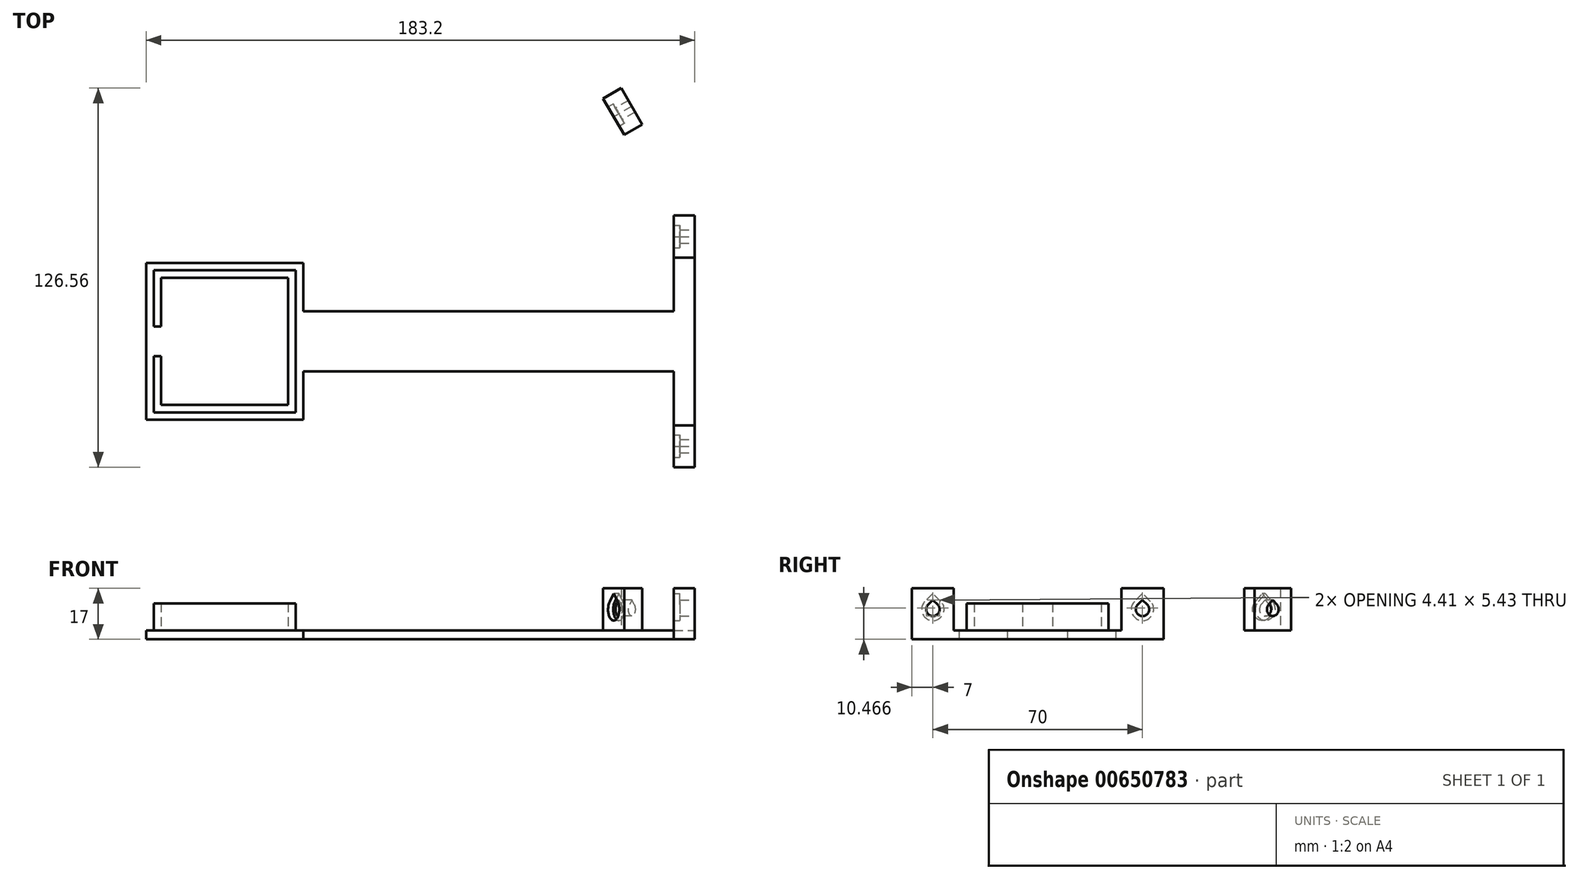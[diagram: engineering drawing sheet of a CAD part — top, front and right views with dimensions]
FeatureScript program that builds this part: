
annotation { "Feature Type Name" : "Feature", "Feature Type Description" : "" }
export const myFeature = defineFeature(function(context is Context, id is Id, definition is map)
    precondition{}
    {
        {
            var Q0;
            Q0=qCreatedBy(makeId("Top.planeOp"),FACE);
            var sketch = newSketch(context, id + "F0", { "sketchPlane" : qUnion([Q0])});
            skLineSegment(sketch, "E0.bottom", {"start": v(21.2, 21.2) * mm, "end": v(-21.2, 21.2) * mm});
            skLineSegment(sketch, "E0.top", {"start": v(21.2, -21.2) * mm, "end": v(-21.2, -21.2) * mm});
            skLineSegment(sketch, "E0.left", {"start": v(21.2, 21.2) * mm, "end": v(21.2, -21.2) * mm});
            skLineSegment(sketch, "E0.right", {"start": v(-21.2, 21.2) * mm, "end": v(-21.2, -21.2) * mm});
            skPoint(sketch, "E0.middle", {"position": v(0, 0) * mm});
            skLineSegment(sketch, "E1.bottom", {"start": v(23.7, 23.7) * mm, "end": v(-23.7, 23.7) * mm});
            skLineSegment(sketch, "E1.top", {"start": v(23.7, -23.7) * mm, "end": v(-23.7, -23.7) * mm});
            skLineSegment(sketch, "E1.left", {"start": v(23.7, 23.7) * mm, "end": v(23.7, -23.7) * mm});
            skLineSegment(sketch, "E1.right", {"start": v(-23.7, 23.7) * mm, "end": v(-23.7, -23.7) * mm});
            skLineSegment(sketch, "E2", {"start": v(0, 0) * mm, "end": v(-23.7, 0) * mm});
            skLineSegment(sketch, "E3", {"start": v(-23.7, 0) * mm, "end": v(-23.7, 5) * mm});
            skLineSegment(sketch, "E4", {"start": v(-21.2, 0) * mm, "end": v(-21.2, -5) * mm});
            skLineSegment(sketch, "E5.bottom", {"start": v(-23.7, 5) * mm, "end": v(-21.2, 5) * mm});
            skLineSegment(sketch, "E5.top", {"start": v(-23.7, -5) * mm, "end": v(-21.2, -5) * mm});
            skLineSegment(sketch, "E5.left", {"start": v(-23.7, 5) * mm, "end": v(-23.7, -5) * mm});
            skLineSegment(sketch, "E5.right", {"start": v(-21.2, 5) * mm, "end": v(-21.2, -5) * mm});
            skLineSegment(sketch, "E6", {"start": v(0, 0) * mm, "end": v(150, 0) * mm});
            skSolve(sketch);
        }
        {
            var Q0;
            {var subQ9=sQuery(id+"F0.wireOp",EDGE,"E0.bottom");Q0=makeQuery(id+"F0.imprint","IMPRINT",FACE,{"disambiguationData":[TD([[makeQuery(id+"F0.imprint","IMPRINT",EDGE,{"derivedFrom":subQ9}),-1.0]])]});}
            var Q1;
            {var subQ2=sQuery(id+"F0.wireOp",EDGE,"E0.top");Q1=makeQuery(id+"F0.imprint","IMPRINT",FACE,{"disambiguationData":[TD([[makeQuery(id+"F0.imprint","IMPRINT",EDGE,{"derivedFrom":subQ2}),1.0]])]});}
            extrude(context, id + "F1", {"entities" : qUnion([Q0, Q1]), "depth" : 9 * mm, "offsetDistance" : 25 * mm});
        }
        {
            var Q0;
            Q0=qCreatedBy(makeId("Top.planeOp"),FACE);
            var sketch = newSketch(context, id + "F2", { "sketchPlane" : qUnion([Q0])});
            skLineSegment(sketch, "E7.bottom", {"start": v(-26.2, -26.2) * mm, "end": v(26.2, -26.2) * mm});
            skLineSegment(sketch, "E7.top", {"start": v(-26.2, 26.2) * mm, "end": v(26.2, 26.2) * mm});
            skLineSegment(sketch, "E7.left", {"start": v(-26.2, -26.2) * mm, "end": v(-26.2, 26.2) * mm});
            skLineSegment(sketch, "E7.right", {"start": v(26.2, -26.2) * mm, "end": v(26.2, 26.2) * mm});
            skPoint(sketch, "E7.middle", {"position": v(0, 0) * mm});
            skLineSegment(sketch, "E8", {"start": v(0, 0) * mm, "end": v(150, 0) * mm});
            skLineSegment(sketch, "E9", {"start": v(150, 0) * mm, "end": v(150, 10) * mm});
            skLineSegment(sketch, "E10", {"start": v(150, 10) * mm, "end": v(26.2, 10) * mm});
            skLineSegment(sketch, "E11", {"start": v(26.2, 10) * mm, "end": v(26.2, -10) * mm});
            skLineSegment(sketch, "E12", {"start": v(26.2, -10) * mm, "end": v(150, -10) * mm});
            skLineSegment(sketch, "E13", {"start": v(150, -10) * mm, "end": v(150, 0) * mm});
            skLineSegment(sketch, "E14", {"start": v(150, 10) * mm, "end": v(157, 10) * mm});
            skLineSegment(sketch, "E15", {"start": v(157, 10) * mm, "end": v(157, -10) * mm});
            skLineSegment(sketch, "E16", {"start": v(157, -10) * mm, "end": v(150, -10) * mm});
            skLineSegment(sketch, "E17", {"start": v(157, 10) * mm, "end": v(157, 35) * mm});
            skLineSegment(sketch, "E18", {"start": v(157, 35) * mm, "end": v(157, 42) * mm});
            skLineSegment(sketch, "E19", {"start": v(157, 42) * mm, "end": v(150, 42) * mm});
            skLineSegment(sketch, "E20", {"start": v(150, 42) * mm, "end": v(150, 10) * mm});
            skLineSegment(sketch, "E21", {"start": v(157, -10) * mm, "end": v(157, -35) * mm});
            skLineSegment(sketch, "E22", {"start": v(157, -35) * mm, "end": v(157, -42) * mm});
            skLineSegment(sketch, "E23", {"start": v(157, -42) * mm, "end": v(150, -42) * mm});
            skLineSegment(sketch, "E24", {"start": v(150, -42) * mm, "end": v(150, -10) * mm});
            skCircle(sketch, "E25.cCircle", {"center": v(0, 0) * mm, "radius": 150 * mm, "construction": true});
            skLineSegment(sketch, "E25.0", {"start": v(150, 40.2) * mm, "end": v(150, -40.2) * mm});
            skLineSegment(sketch, "E25.1", {"start": v(150, -40.2) * mm, "end": v(109.8, -109.8) * mm});
            skLineSegment(sketch, "E25.2", {"start": v(109.8, -109.8) * mm, "end": v(40.2, -150) * mm});
            skLineSegment(sketch, "E25.3", {"start": v(40.2, -150) * mm, "end": v(-40.2, -150) * mm});
            skLineSegment(sketch, "E25.4", {"start": v(-40.2, -150) * mm, "end": v(-109.8, -109.8) * mm});
            skLineSegment(sketch, "E25.5", {"start": v(-109.8, -109.8) * mm, "end": v(-150, -40.2) * mm});
            skLineSegment(sketch, "E25.6", {"start": v(-150, -40.2) * mm, "end": v(-150, 40.2) * mm});
            skLineSegment(sketch, "E25.7", {"start": v(-150, 40.2) * mm, "end": v(-109.8, 109.8) * mm});
            skLineSegment(sketch, "E25.8", {"start": v(-109.8, 109.8) * mm, "end": v(-40.2, 150) * mm});
            skLineSegment(sketch, "E25.9", {"start": v(-40.2, 150) * mm, "end": v(40.2, 150) * mm});
            skLineSegment(sketch, "E25.10", {"start": v(40.2, 150) * mm, "end": v(109.8, 109.8) * mm});
            skLineSegment(sketch, "E25.11", {"start": v(109.8, 109.8) * mm, "end": v(150, 40.2) * mm});
            skPoint(sketch, "E25.0.midPoint", {"position": v(150, 0) * mm});
            skLineSegment(sketch, "E26", {"start": v(129.9, 75) * mm, "end": v(0, 0) * mm});
            skLineSegment(sketch, "E27", {"start": v(129.9, 75) * mm, "end": v(126.4, 81.06) * mm});
            skLineSegment(sketch, "E28", {"start": v(129.9, 75) * mm, "end": v(133.4, 68.94) * mm});
            skLineSegment(sketch, "E29", {"start": v(133.4, 68.94) * mm, "end": v(31.32, 10) * mm});
            skLineSegment(sketch, "E30", {"start": v(133.4, 68.94) * mm, "end": v(139.47, 72.44) * mm});
            skLineSegment(sketch, "E31", {"start": v(126.4, 81.06) * mm, "end": v(26.2, 23.2) * mm});
            skLineSegment(sketch, "E32", {"start": v(139.47, 72.44) * mm, "end": v(132.47, 84.56) * mm});
            skLineSegment(sketch, "E33", {"start": v(132.47, 84.56) * mm, "end": v(126.4, 81.06) * mm});
            skSolve(sketch);
        }
        {
            var Q0;
            Q0=makeQuery(id+"F2.imprint","IMPRINT",FACE,{"disambiguationData":[TD([[makeQuery(id+"F2.imprint","IMPRINT",EDGE,{"derivedFrom":sQuery(id+"F2.wireOp",EDGE,"E7.bottom")}),1.0]])]});
            var Q1;
            Q1=makeQuery(id+"F2.imprint","IMPRINT",FACE,{"disambiguationData":[TD([[makeQuery(id+"F2.imprint","IMPRINT",EDGE,{"derivedFrom":sQuery(id+"F2.wireOp",EDGE,"E14")}),1.0]])]});
            var Q2;
            {var subQ0=sQuery(id+"F2.wireOp",EDGE,"E9");Q2=makeQuery(id+"F2.imprint","IMPRINT",FACE,{"disambiguationData":[TD([[makeQuery(id+"F2.imprint","IMPRINT",EDGE,{"derivedFrom":subQ0}),1.0]])]});}
            var Q3;
            Q3=makeQuery(id+"F2.imprint","IMPRINT",FACE,{"disambiguationData":[TD([[makeQuery(id+"F2.imprint","IMPRINT",EDGE,{"derivedFrom":sQuery(id+"F2.wireOp",EDGE,"E9")}),-1.0]])]});
            var Q4;
            Q4=makeQuery(id+"F2.imprint","IMPRINT",FACE,{"disambiguationData":[TD([[makeQuery(id+"F2.imprint","IMPRINT",EDGE,{"derivedFrom":sQuery(id+"F2.wireOp",EDGE,"E16")}),1.0]])]});
            var Q5;
            {var subQ4=sQuery(id+"F2.wireOp",EDGE,"E12");Q5=makeQuery(id+"F2.imprint","IMPRINT",FACE,{"disambiguationData":[TD([[makeQuery(id+"F2.imprint","IMPRINT",EDGE,{"derivedFrom":subQ4}),1.0]])]});}
            var Q6;
            {var subQ3=sQuery(id+"F2.wireOp",EDGE,"E8");var subQ6=sQuery(id+"F2.wireOp",EDGE,"E25.0");var subQ8=makeQuery(id+"F2.imprint","INTERSECT",VERTEX,{"derivedFrom":[subQ3,subQ6]});Q6=makeQuery(id+"F2.imprint","IMPRINT",FACE,{"disambiguationData":[TD([[makeQuery(id+"F2.imprint","IMPRINT",EDGE,{"disambiguationData":[TD([[subQ8,1.0]])],"derivedFrom":subQ3}),1.0]])]});}
            var Q7;
            {var subQ2=sQuery(id+"F2.wireOp",EDGE,"E14");Q7=makeQuery(id+"F2.imprint","IMPRINT",FACE,{"disambiguationData":[TD([[makeQuery(id+"F2.imprint","IMPRINT",EDGE,{"derivedFrom":subQ2}),-1.0]])]});}
            var Q8;
            {var subQ3=sQuery(id+"F2.wireOp",EDGE,"E26");var subQ5=sQuery(id+"F2.wireOp",EDGE,"E8");var subQ6=makeQuery(id+"F2.imprint","INTERSECT",VERTEX,{"derivedFrom":[subQ5,subQ3]});Q8=makeQuery(id+"F2.imprint","IMPRINT",FACE,{"disambiguationData":[TD([[makeQuery(id+"F2.imprint","IMPRINT",EDGE,{"disambiguationData":[TD([[subQ6,-1.0]])],"derivedFrom":subQ5}),1.0]])]});}
            var Q9;
            {var subQ0=sQuery(id+"F2.wireOp",EDGE,"E27");Q9=makeQuery(id+"F2.imprint","IMPRINT",FACE,{"disambiguationData":[TD([[makeQuery(id+"F2.imprint","IMPRINT",EDGE,{"derivedFrom":subQ0}),1.0]])]});}
            var Q10;
            {var subQ0=sQuery(id+"F2.wireOp",EDGE,"E28");Q10=makeQuery(id+"F2.imprint","IMPRINT",FACE,{"disambiguationData":[TD([[makeQuery(id+"F2.imprint","IMPRINT",EDGE,{"derivedFrom":subQ0}),-1.0]])]});}
            var Q11;
            Q11=makeQuery(id+"F2.imprint","IMPRINT",FACE,{"disambiguationData":[TD([[makeQuery(id+"F2.imprint","IMPRINT",EDGE,{"derivedFrom":sQuery(id+"F2.wireOp",EDGE,"E27")}),-1.0]])]});
            extrude(context, id + "F3", {"entities" : qUnion([Q0, Q1, Q2, Q3, Q4, Q5, Q6, Q7, Q8, Q9, Q10, Q11]), "operationType" : NewBodyOperationType.ADD, "oppositeDirection" : true, "depth" : 3 * mm, "offsetDistance" : 25 * mm});
        }
        {
            var Q0;
            Q0=makeQuery(id+"F3.opExtrude","SWEPT_FACE",FACE,{"disambiguationData":[OSD([sQuery(id+"F2.wireOp",EDGE,"E15"),sQuery(id+"F2.wireOp",EDGE,"E17"),sQuery(id+"F2.wireOp",EDGE,"E18"),sQuery(id+"F2.wireOp",EDGE,"E21"),sQuery(id+"F2.wireOp",EDGE,"E22")])]});
            var sketch = newSketch(context, id + "F4", { "sketchPlane" : qUnion([Q0])});
            skPoint(sketch, "E34.0", {"position": v(-35, 0) * mm});
            skPoint(sketch, "E35.0", {"position": v(35, 0) * mm});
            skLineSegment(sketch, "E36", {"start": v(35, 0) * mm, "end": v(28, 0) * mm});
            skLineSegment(sketch, "E37", {"start": v(28, 0) * mm, "end": v(28, 14) * mm});
            skLineSegment(sketch, "E38", {"start": v(28, 14) * mm, "end": v(42, 14) * mm});
            skLineSegment(sketch, "E39", {"start": v(42, 14) * mm, "end": v(42, 0) * mm});
            skLineSegment(sketch, "E40", {"start": v(35, 0) * mm, "end": v(35, 7) * mm});
            skCircle(sketch, "E41", {"center": v(35, 7) * mm, "radius": 2.25 * mm});
            skLineSegment(sketch, "E42", {"start": v(-35, 0) * mm, "end": v(-35, 7) * mm});
            skLineSegment(sketch, "E43.bottom", {"start": v(-28, 14) * mm, "end": v(-42, 14) * mm});
            skLineSegment(sketch, "E43.top", {"start": v(-28, 0) * mm, "end": v(-42, 0) * mm});
            skLineSegment(sketch, "E43.left", {"start": v(-28, 14) * mm, "end": v(-28, 0) * mm});
            skLineSegment(sketch, "E43.right", {"start": v(-42, 14) * mm, "end": v(-42, 0) * mm});
            skPoint(sketch, "E43.middle", {"position": v(-35, 7) * mm});
            skCircle(sketch, "E44", {"center": v(-35, 7) * mm, "radius": 2.25 * mm});
            skLineSegment(sketch, "E45", {"start": v(-35, 7) * mm, "end": v(-37.25, 7) * mm});
            skLineSegment(sketch, "E46", {"start": v(-37.25, 7) * mm, "end": v(-35, 9.25) * mm});
            skLineSegment(sketch, "E47", {"start": v(-35, 7) * mm, "end": v(-36.6, 8.6) * mm});
            skLineSegment(sketch, "E48", {"start": v(-36.6, 8.6) * mm, "end": v(-35, 10.18) * mm});
            skLineSegment(sketch, "E49", {"start": v(-35, 10.18) * mm, "end": v(-33.4, 8.6) * mm});
            skLineSegment(sketch, "E50", {"start": v(35, 7) * mm, "end": v(32.75, 7) * mm});
            skLineSegment(sketch, "E51", {"start": v(32.75, 7) * mm, "end": v(35, 9.25) * mm});
            skLineSegment(sketch, "E52", {"start": v(35, 7) * mm, "end": v(33.4, 8.6) * mm});
            skLineSegment(sketch, "E53", {"start": v(33.4, 8.6) * mm, "end": v(35, 10.18) * mm});
            skLineSegment(sketch, "E54", {"start": v(35, 10.18) * mm, "end": v(36.6, 8.6) * mm});
            skSolve(sketch);
        }
        {
            var Q0;
            {var subQ1=sQuery(id+"F4.wireOp",EDGE,"E36");Q0=makeQuery(id+"F4.imprint","IMPRINT",FACE,{"disambiguationData":[TD([[makeQuery(id+"F4.imprint","IMPRINT",EDGE,{"derivedFrom":subQ1}),1.0]])]});}
            var Q1;
            Q1=makeQuery(id+"F4.imprint","IMPRINT",FACE,{"disambiguationData":[TD([[makeQuery(id+"F4.imprint","IMPRINT",EDGE,{"derivedFrom":sQuery(id+"F4.wireOp",EDGE,"E43.bottom")}),1.0]])]});
            extrude(context, id + "F5", {"entities" : qUnion([Q0, Q1]), "operationType" : NewBodyOperationType.ADD, "oppositeDirection" : true, "depth" : 5 * mm, "offsetDistance" : 25 * mm});
        }
        {
            var Q0;
            Q0=makeQuery(id+"F5.opExtrude","CAP_FACE",FACE,{"disambiguationData":[OSD([sQuery(id+"F2.wireOp",EDGE,"E15"),sQuery(id+"F2.wireOp",EDGE,"E17"),sQuery(id+"F2.wireOp",EDGE,"E18"),sQuery(id+"F2.wireOp",EDGE,"E21"),sQuery(id+"F2.wireOp",EDGE,"E22"),sQuery(id+"F4.wireOp",EDGE,"E36"),sQuery(id+"F4.wireOp",EDGE,"E37"),sQuery(id+"F4.wireOp",EDGE,"E38"),sQuery(id+"F4.wireOp",EDGE,"E39"),sQuery(id+"F4.wireOp",EDGE,"E41")])],"isStart":false});
            var sketch = newSketch(context, id + "F6", { "sketchPlane" : qUnion([Q0])});
            skPoint(sketch, "E55.0", {"position": v(-35, 7) * mm});
            skLineSegment(sketch, "E56.bottom", {"start": v(-42, 0) * mm, "end": v(-28, 0) * mm});
            skLineSegment(sketch, "E56.top", {"start": v(-42, 14) * mm, "end": v(-28, 14) * mm});
            skLineSegment(sketch, "E56.left", {"start": v(-42, 0) * mm, "end": v(-42, 14) * mm});
            skLineSegment(sketch, "E56.right", {"start": v(-28, 0) * mm, "end": v(-28, 14) * mm});
            skCircle(sketch, "E57", {"center": v(-35, 7) * mm, "radius": 3.75 * mm});
            skPoint(sketch, "E58.0", {"position": v(35, 7) * mm});
            skLineSegment(sketch, "E59.bottom", {"start": v(28, 0) * mm, "end": v(42, 0) * mm});
            skLineSegment(sketch, "E59.top", {"start": v(28, 14) * mm, "end": v(42, 14) * mm});
            skLineSegment(sketch, "E59.left", {"start": v(28, 0) * mm, "end": v(28, 14) * mm});
            skLineSegment(sketch, "E59.right", {"start": v(42, 0) * mm, "end": v(42, 14) * mm});
            skCircle(sketch, "E60", {"center": v(35, 7) * mm, "radius": 3.75 * mm});
            skLineSegment(sketch, "E61", {"start": v(35, 7) * mm, "end": v(31.25, 7) * mm});
            skLineSegment(sketch, "E62", {"start": v(31.25, 7) * mm, "end": v(35, 10.75) * mm});
            skLineSegment(sketch, "E63", {"start": v(35, 7) * mm, "end": v(32.35, 9.65) * mm});
            skLineSegment(sketch, "E64", {"start": v(32.35, 9.65) * mm, "end": v(35, 12.3) * mm});
            skLineSegment(sketch, "E65", {"start": v(35, 12.3) * mm, "end": v(37.65, 9.65) * mm});
            skLineSegment(sketch, "E66", {"start": v(-35, 7) * mm, "end": v(-38.75, 7) * mm});
            skLineSegment(sketch, "E67", {"start": v(-38.75, 7) * mm, "end": v(-35, 10.75) * mm});
            skLineSegment(sketch, "E68", {"start": v(-35, 7) * mm, "end": v(-37.65, 9.65) * mm});
            skLineSegment(sketch, "E69", {"start": v(-37.65, 9.65) * mm, "end": v(-35, 12.3) * mm});
            skLineSegment(sketch, "E70", {"start": v(-35, 12.3) * mm, "end": v(-32.35, 9.65) * mm});
            skSolve(sketch);
        }
        {
            var Q0;
            Q0=makeQuery(id+"F6.imprint","IMPRINT",FACE,{"disambiguationData":[TD([[makeQuery(id+"F6.imprint","IMPRINT",EDGE,{"derivedFrom":sQuery(id+"F6.wireOp",EDGE,"E56.bottom")}),-1.0]])]});
            var Q1;
            Q1=makeQuery(id+"F6.imprint","IMPRINT",FACE,{"disambiguationData":[TD([[makeQuery(id+"F6.imprint","IMPRINT",EDGE,{"derivedFrom":sQuery(id+"F6.wireOp",EDGE,"E59.bottom")}),1.0]])]});
            extrude(context, id + "F7", {"entities" : qUnion([Q0, Q1]), "operationType" : NewBodyOperationType.ADD, "depth" : 2 * mm, "offsetDistance" : 25 * mm});
        }
        {
            var Q0;
            Q0=sQuery(id+"F2.wireOp",EDGE,"E26");
            var Q1;
            Q1=sQuery(id+"F2.wireOp",VERTEX,"E27.start");
            cPlane(context, id + "F8", {"entities" : qUnion([Q0, Q1]), "cplaneType" : CPlaneType.LINE_POINT, "offset" : 25 * mm, "width" : 150 * mm, "height" : 150 * mm});
        }
        {
            var Q0;
            Q0=qCreatedBy(id+"F8.planeOp",FACE);
            var sketch = newSketch(context, id + "F9", { "sketchPlane" : qUnion([Q0])});
            skPoint(sketch, "E71.0", {"position": v(0, 0) * mm});
            skLineSegment(sketch, "E72", {"start": v(0, 0) * mm, "end": v(0, 7) * mm});
            skLineSegment(sketch, "E73.bottom", {"start": v(-7, 14) * mm, "end": v(7, 14) * mm});
            skLineSegment(sketch, "E73.top", {"start": v(-7, 0) * mm, "end": v(7, 0) * mm});
            skLineSegment(sketch, "E73.left", {"start": v(-7, 14) * mm, "end": v(-7, 0) * mm});
            skLineSegment(sketch, "E73.right", {"start": v(7, 14) * mm, "end": v(7, 0) * mm});
            skPoint(sketch, "E73.middle", {"position": v(0, 7) * mm});
            skCircle(sketch, "E74", {"center": v(0, 7) * mm, "radius": 3.75 * mm});
            skLineSegment(sketch, "E75", {"start": v(0, 7) * mm, "end": v(3.75, 7) * mm});
            skLineSegment(sketch, "E76", {"start": v(3.75, 7) * mm, "end": v(0, 10.75) * mm});
            skLineSegment(sketch, "E77", {"start": v(0, 7) * mm, "end": v(2.65, 9.65) * mm});
            skLineSegment(sketch, "E78", {"start": v(2.65, 9.65) * mm, "end": v(0, 12.3) * mm});
            skLineSegment(sketch, "E79", {"start": v(0, 12.3) * mm, "end": v(-2.65, 9.65) * mm});
            skSolve(sketch);
        }
        {
            var Q0;
            Q0=makeQuery(id+"F9.imprint","IMPRINT",FACE,{"disambiguationData":[TD([[makeQuery(id+"F9.imprint","IMPRINT",EDGE,{"derivedFrom":sQuery(id+"F9.wireOp",EDGE,"E73.bottom")}),-1.0]])]});
            extrude(context, id + "F10", {"entities" : qUnion([Q0]), "operationType" : NewBodyOperationType.ADD, "oppositeDirection" : true, "depth" : 2 * mm, "offsetDistance" : 25 * mm});
        }
        {
            var Q0;
            Q0=makeQuery(id+"F10.opExtrude","CAP_FACE",FACE,{"disambiguationData":[OSD([sQuery(id+"F9.wireOp",EDGE,"E73.bottom"),sQuery(id+"F9.wireOp",EDGE,"E73.top"),sQuery(id+"F9.wireOp",EDGE,"E73.left"),sQuery(id+"F9.wireOp",EDGE,"E73.right"),sQuery(id+"F9.wireOp",EDGE,"E74"),sQuery(id+"F9.wireOp",EDGE,"E78"),sQuery(id+"F9.wireOp",EDGE,"E79")])],"isStart":false});
            var sketch = newSketch(context, id + "F11", { "sketchPlane" : qUnion([Q0])});
            skPoint(sketch, "E80.0", {"position": v(0, 7) * mm});
            skLineSegment(sketch, "E81.bottom", {"start": v(7, 14) * mm, "end": v(-7, 14) * mm});
            skLineSegment(sketch, "E81.top", {"start": v(7, 0) * mm, "end": v(-7, 0) * mm});
            skLineSegment(sketch, "E81.left", {"start": v(7, 14) * mm, "end": v(7, 0) * mm});
            skLineSegment(sketch, "E81.right", {"start": v(-7, 14) * mm, "end": v(-7, 0) * mm});
            skCircle(sketch, "E82", {"center": v(0, 7) * mm, "radius": 2.25 * mm});
            skLineSegment(sketch, "E83", {"start": v(0, 7) * mm, "end": v(-2.25, 7) * mm});
            skLineSegment(sketch, "E84", {"start": v(-2.25, 7) * mm, "end": v(0, 9.25) * mm});
            skLineSegment(sketch, "E85", {"start": v(0, 7) * mm, "end": v(-1.6, 8.6) * mm});
            skLineSegment(sketch, "E86", {"start": v(-1.6, 8.6) * mm, "end": v(0, 10.18) * mm});
            skLineSegment(sketch, "E87", {"start": v(0, 10.18) * mm, "end": v(1.6, 8.6) * mm});
            skSolve(sketch);
        }
        {
            var Q0;
            {var subQ1=sQuery(id+"F11.wireOp",EDGE,"E86");Q0=makeQuery(id+"F11.imprint","IMPRINT",FACE,{"disambiguationData":[TD([[makeQuery(id+"F11.imprint","IMPRINT",EDGE,{"derivedFrom":subQ1}),1.0]])]});}
            var Q1;
            Q1=makeQuery(id+"F11.imprint","IMPRINT",FACE,{"disambiguationData":[TD([[makeQuery(id+"F11.imprint","IMPRINT",EDGE,{"derivedFrom":sQuery(id+"F11.wireOp",EDGE,"E81.bottom")}),1.0]])]});
            extrude(context, id + "F12", {"entities" : qUnion([Q0, Q1]), "operationType" : NewBodyOperationType.ADD, "depth" : 5 * mm, "offsetDistance" : 25 * mm});
        }
    });
